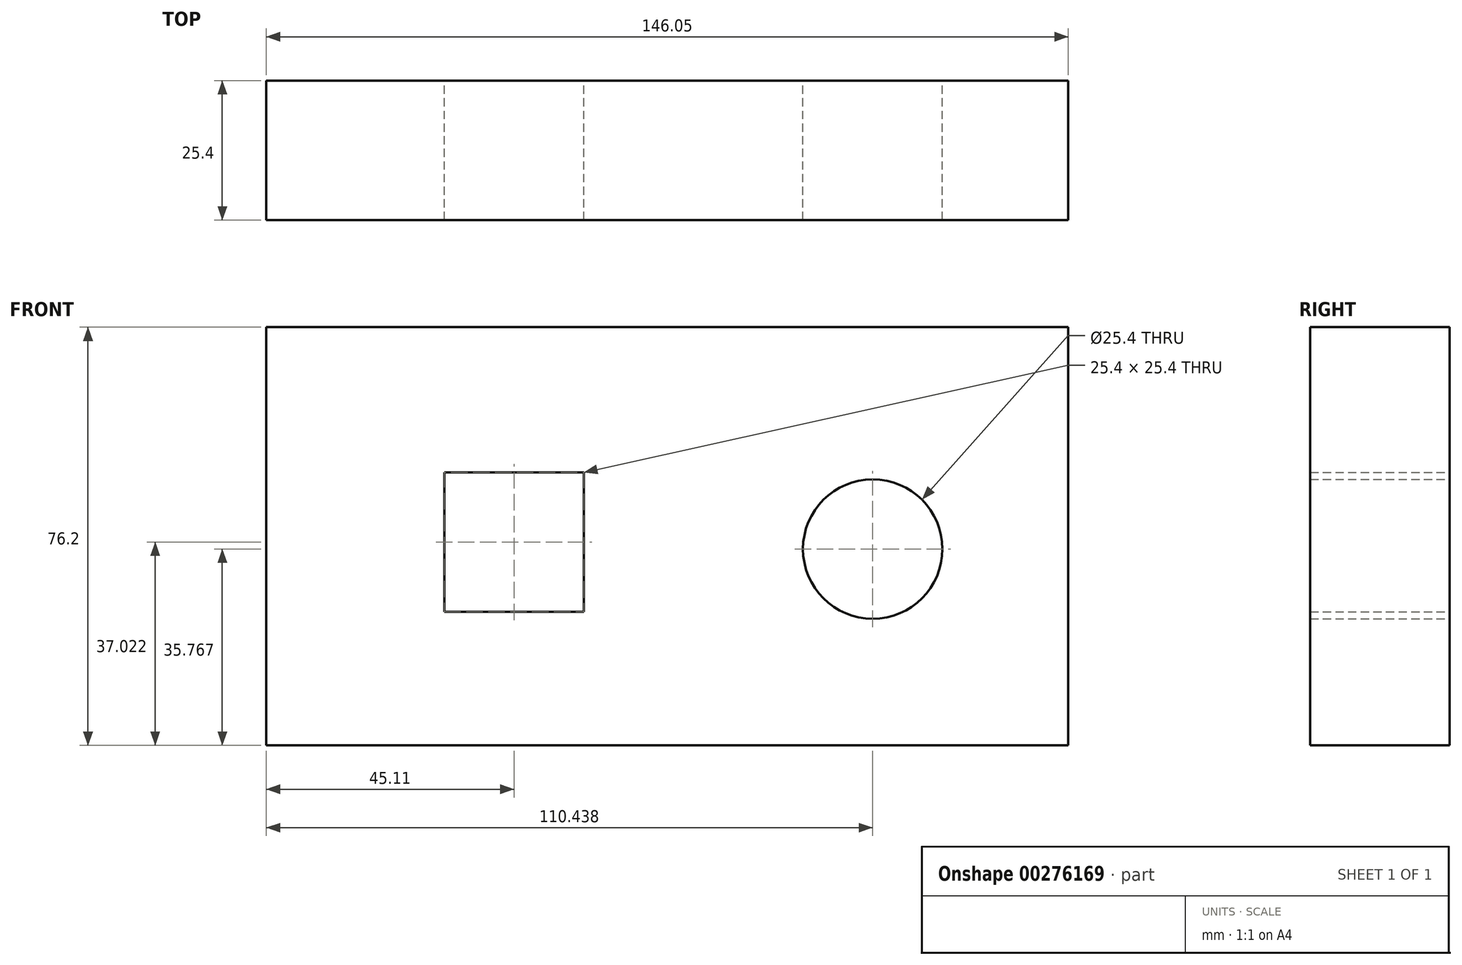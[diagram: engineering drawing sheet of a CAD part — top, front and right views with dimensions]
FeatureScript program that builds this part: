
annotation { "Feature Type Name" : "Feature", "Feature Type Description" : "" }
export const myFeature = defineFeature(function(context is Context, id is Id, definition is map)
    precondition{}
    {
        {
            var Q0;
            Q0=qCreatedBy(makeId("Front.planeOp"),FACE);
            var sketch = newSketch(context, id + "F0", { "sketchPlane" : qUnion([Q0])});
            skLineSegment(sketch, "E0.bottom", {"start": v(88.24, 0) * mm, "end": v(-57.81, 0) * mm});
            skLineSegment(sketch, "E0.top", {"start": v(88.24, 76.2) * mm, "end": v(-57.81, 76.2) * mm});
            skLineSegment(sketch, "E0.left", {"start": v(88.24, 0) * mm, "end": v(88.24, 76.2) * mm});
            skLineSegment(sketch, "E0.right", {"start": v(-57.81, 0) * mm, "end": v(-57.81, 76.2) * mm});
            skLineSegment(sketch, "E1.bottom", {"start": v(-25.4, 49.72) * mm, "end": v(0, 49.72) * mm});
            skLineSegment(sketch, "E1.top", {"start": v(-25.4, 24.32) * mm, "end": v(0, 24.32) * mm});
            skLineSegment(sketch, "E1.left", {"start": v(-25.4, 49.72) * mm, "end": v(-25.4, 24.32) * mm});
            skLineSegment(sketch, "E1.right", {"start": v(0, 49.72) * mm, "end": v(0, 24.32) * mm});
            skCircle(sketch, "E2", {"center": v(52.63, 35.77) * mm, "radius": 12.7 * mm});
            skSolve(sketch);
        }
        {
            var Q0;
            Q0=makeQuery(id+"F0.imprint","IMPRINT",FACE,{"disambiguationData":[TD([[makeQuery(id+"F0.imprint","IMPRINT",EDGE,{"derivedFrom":sQuery(id+"F0.wireOp",EDGE,"E0.bottom")}),-1.0]])]});
            extrude(context, id + "F1", {"entities" : qUnion([Q0]), "depth" : 25.4 * mm});
        }
    });
